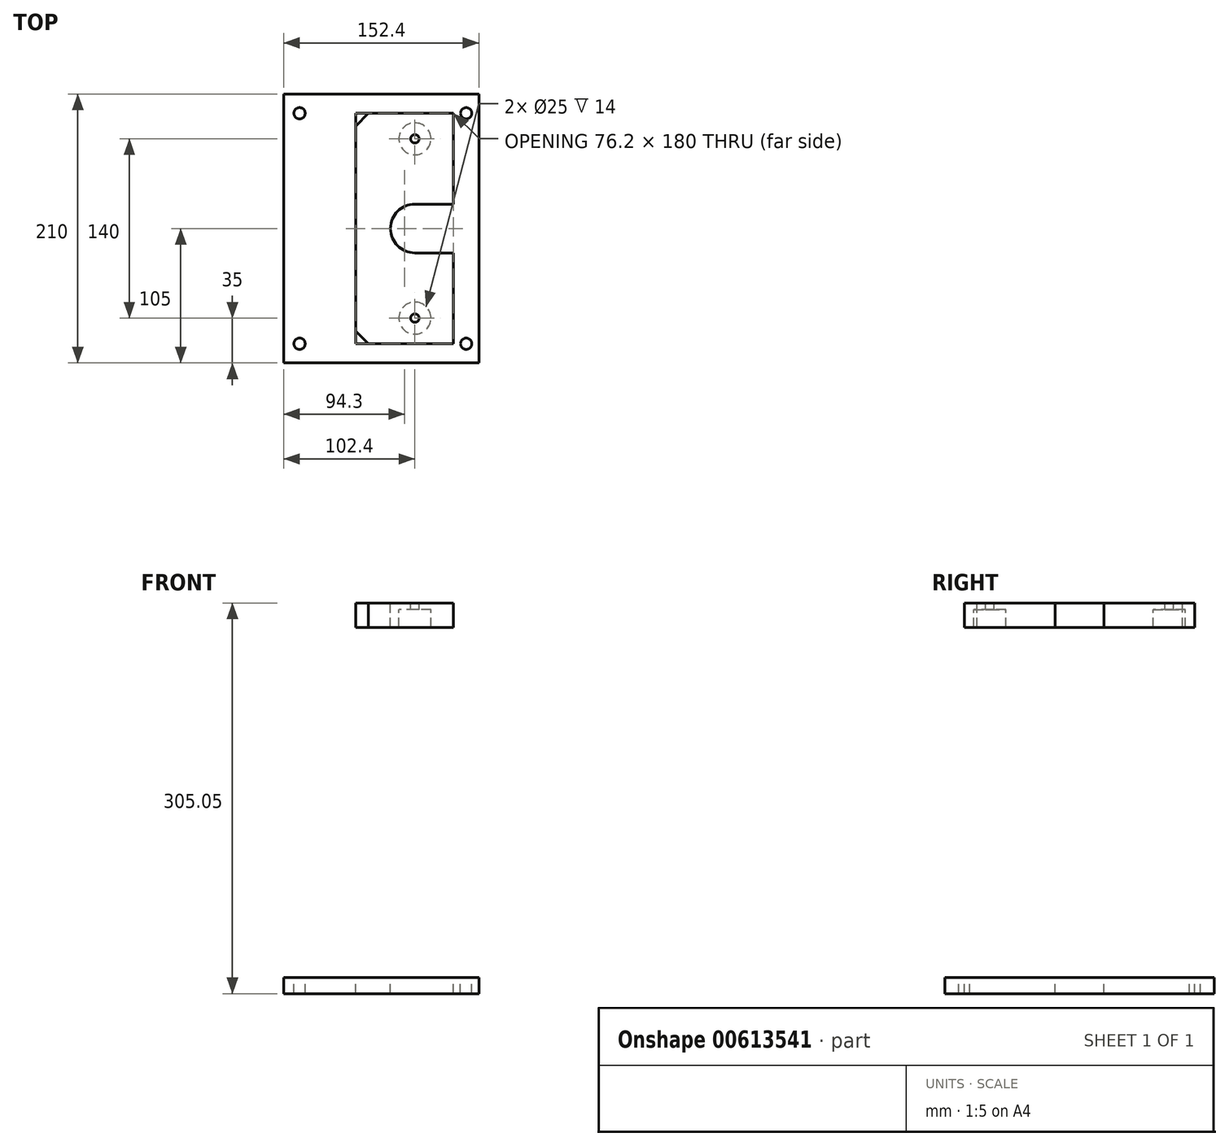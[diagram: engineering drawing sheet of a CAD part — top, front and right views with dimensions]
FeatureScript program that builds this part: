
annotation { "Feature Type Name" : "Feature", "Feature Type Description" : "" }
export const myFeature = defineFeature(function(context is Context, id is Id, definition is map)
    precondition{}
    {
        {
            var Q0;
            Q0=qCreatedBy(makeId("Top.planeOp"),FACE);
            cPlane(context, id + "F0", {"entities" : qUnion([Q0]), "cplaneType" : CPlaneType.OFFSET, "offset" : 12.7 * mm, "width" : 150 * mm, "height" : 150 * mm});
        }
        {
            var Q0;
            Q0=qCreatedBy(makeId("Top.planeOp"),FACE);
            cPlane(context, id + "F1", {"entities" : qUnion([Q0]), "cplaneType" : CPlaneType.OFFSET, "offset" : 300 * mm, "width" : 150 * mm, "height" : 150 * mm});
        }
        {
            var Q0;
            Q0=qCreatedBy(makeId("Top.planeOp"),FACE);
            var sketch = newSketch(context, id + "F2", { "sketchPlane" : qUnion([Q0])});
            skLineSegment(sketch, "E0.bottom", {"start": v(50, 105) * mm, "end": v(-102.4, 105) * mm});
            skLineSegment(sketch, "E0.top", {"start": v(50, -105) * mm, "end": v(-102.4, -105) * mm});
            skLineSegment(sketch, "E0.left", {"start": v(50, 105) * mm, "end": v(50, -105) * mm});
            skLineSegment(sketch, "E0.right", {"start": v(-102.4, 105) * mm, "end": v(-102.4, -105) * mm});
            skCircle(sketch, "E1", {"center": v(0, 70) * mm, "radius": 12.5 * mm, "construction": true});
            skCircle(sketch, "E2", {"center": v(0, -70) * mm, "radius": 12.5 * mm, "construction": true});
            skSolve(sketch);
        }
        {
            var Q0;
            Q0=qCreatedBy(id+"F1.planeOp",FACE);
            var sketch = newSketch(context, id + "F3", { "sketchPlane" : qUnion([Q0])});
            skLineSegment(sketch, "E3.bottom", {"start": v(30, 90) * mm, "end": v(-46.2, 90) * mm});
            skLineSegment(sketch, "E3.top", {"start": v(30, -90) * mm, "end": v(-46.2, -90) * mm});
            skLineSegment(sketch, "E3.left", {"start": v(30, 90) * mm, "end": v(30, 19.05) * mm});
            skLineSegment(sketch, "E3.right", {"start": v(-46.2, 90) * mm, "end": v(-46.2, -90) * mm});
            skArc(sketch, "E4", {"start": v(0, 19.05) * mm, "mid": v(-19.05, 0) * mm, "end": v(0, -19.05) * mm});
            skLineSegment(sketch, "E5", {"start": v(0, 19.05) * mm, "end": v(30, 19.05) * mm});
            skLineSegment(sketch, "E6", {"start": v(0, -19.05) * mm, "end": v(30, -19.05) * mm});
            skLineSegment(sketch, "E7.trimOffspring", {"start": v(30, -19.05) * mm, "end": v(30, -90) * mm});
            skSolve(sketch);
        }
        {
            var Q0;
            Q0 = qSketchRegion(id + "F2", true);
            var Q1;
            Q1=qCreatedBy(id+"F0.planeOp",FACE);
            extrude(context, id + "F4", {"entities" : qUnion([Q0]), "endBound" : BoundingType.UP_TO_SURFACE, "depth" : 12.7 * mm, "endBoundEntityFace" : qUnion([Q1]), "offsetDistance" : 25 * mm});
        }
        {
            var Q0;
            Q0=qCreatedBy(id+"F0.planeOp",FACE);
            var sketch = newSketch(context, id + "F5", { "sketchPlane" : qUnion([Q0])});
            skCircle(sketch, "E8", {"center": v(0, 70) * mm, "radius": 12.5 * mm});
            skCircle(sketch, "E9", {"center": v(0, -70) * mm, "radius": 12.5 * mm});
            skSolve(sketch);
        }
        {
            var Q0;
            Q0=makeQuery(id+"F5.imprint","IMPRINT",FACE,{"disambiguationData":[TD([[makeQuery(id+"F5.imprint","IMPRINT",EDGE,{"derivedFrom":sQuery(id+"F5.wireOp",EDGE,"E8")}),1.0]])]});
            var Q1;
            Q1=qCreatedBy(id+"F1.planeOp",FACE);
            extrude(context, id + "F6", {"entities" : qUnion([Q0]), "endBound" : BoundingType.UP_TO_SURFACE, "depth" : 25 * mm, "endBoundEntityFace" : qUnion([Q1]), "offsetDistance" : 25 * mm});
        }
        {
            var Q0;
            Q0=makeQuery(id+"F5.imprint","IMPRINT",FACE,{"disambiguationData":[TD([[makeQuery(id+"F5.imprint","IMPRINT",EDGE,{"derivedFrom":sQuery(id+"F5.wireOp",EDGE,"E9")}),1.0]])]});
            var Q1;
            Q1=qCreatedBy(id+"F1.planeOp",FACE);
            extrude(context, id + "F7", {"entities" : qUnion([Q0]), "endBound" : BoundingType.UP_TO_SURFACE, "depth" : 25 * mm, "endBoundEntityFace" : qUnion([Q1]), "offsetDistance" : 25 * mm});
        }
        {
            var Q0;
            Q0=makeQuery(id+"F6.opExtrude","CAP_EDGE",EDGE,{"disambiguationData":[OSD([sQuery(id+"F5.wireOp",EDGE,"E8")])],"isStart":true});
            var Q1;
            Q1=makeQuery(id+"F6.opExtrude","CAP_EDGE",EDGE,{"disambiguationData":[OSD([sQuery(id+"F5.wireOp",EDGE,"E8")])],"isStart":false});
            chamfer(context, id + "F8", {"entities" : qUnion([Q0, Q1]), "width" : 1 * mm, "tangentPropagation" : true});
        }
        {
            var Q0;
            Q0=makeQuery(id+"F7.opExtrude","CAP_EDGE",EDGE,{"disambiguationData":[OSD([sQuery(id+"F5.wireOp",EDGE,"E9")])],"isStart":true});
            var Q1;
            Q1=makeQuery(id+"F7.opExtrude","CAP_EDGE",EDGE,{"disambiguationData":[OSD([sQuery(id+"F5.wireOp",EDGE,"E9")])],"isStart":false});
            chamfer(context, id + "F9", {"entities" : qUnion([Q0, Q1]), "width" : 1 * mm, "tangentPropagation" : true});
        }
        {
            var Q0;
            Q0=sQuery(id+"F5.wireOp",VERTEX,"E8.center");
            var Q1;
            Q1=makeQuery(id+"F6.opExtrude","SWEPT_BODY",BODY,{"disambiguationData":[OSD([sQuery(id+"F5.wireOp",EDGE,"E8")])]});
            hole(context, id + "F10", {"style" : HoleStyle.SIMPLE, "endStyle" : HoleEndStyle.BLIND, "oppositeDirection" : true, "standardTappedOrClearance" : lookupTablePath({ "standard" : "ISO", "engagement" : "75%", "pitch" : "1 mm", "size" : "M6", "type" : "Tapped" }), "standardBlindInLast" : lookupTablePath({ "standard" : "ISO", "engagement" : "75%", "pitch" : "1 mm", "size" : "M6", "type" : "Tapped" }), "holeDiameter" : 5 * mm, "majorDiameter" : 6 * mm, "showTappedDepth" : true, "holeDepth" : 15 * mm, "isTappedThrough" : true, "tappedDepth" : 12 * mm, "tapClearance" : 3, "locations" : qUnion([Q0]), "scope" : qUnion([Q1])});
        }
        {
            var Q0;
            Q0=sQuery(id+"F5.wireOp",VERTEX,"E9.center");
            var Q1;
            Q1=makeQuery(id+"F7.opExtrude","SWEPT_BODY",BODY,{"disambiguationData":[OSD([sQuery(id+"F5.wireOp",EDGE,"E9")])]});
            hole(context, id + "F11", {"style" : HoleStyle.SIMPLE, "endStyle" : HoleEndStyle.BLIND, "oppositeDirection" : true, "standardTappedOrClearance" : lookupTablePath({ "standard" : "ISO", "engagement" : "75%", "pitch" : "1 mm", "size" : "M6", "type" : "Tapped" }), "standardBlindInLast" : lookupTablePath({ "standard" : "ISO", "engagement" : "75%", "pitch" : "1 mm", "size" : "M6", "type" : "Tapped" }), "holeDiameter" : 5 * mm, "majorDiameter" : 6 * mm, "showTappedDepth" : true, "holeDepth" : 15 * mm, "isTappedThrough" : true, "tappedDepth" : 12 * mm, "tapClearance" : 3, "locations" : qUnion([Q0]), "scope" : qUnion([Q1])});
        }
        {
            var Q0;
            Q0=sQuery(id+"F2.wireOp",VERTEX,"E2.center");
            var Q1;
            Q1=sQuery(id+"F2.wireOp",VERTEX,"E1.center");
            var Q2;
            Q2=makeQuery(id+"F4.opExtrude","SWEPT_BODY",BODY,{"disambiguationData":[OSD([sQuery(id+"F2.wireOp",EDGE,"E0.bottom"),sQuery(id+"F2.wireOp",EDGE,"E0.top"),sQuery(id+"F2.wireOp",EDGE,"E0.left"),sQuery(id+"F2.wireOp",EDGE,"E0.right")])]});
            hole(context, id + "F12", {"style" : HoleStyle.C_BORE, "endStyle" : HoleEndStyle.BLIND, "oppositeDirection" : true, "standardTappedOrClearance" : lookupTablePath({ "standard" : "ISO", "fit" : "Normal", "size" : "M6", "type" : "Clearance" }), "standardBlindInLast" : lookupTablePath({ "fit" : "Standard", "standard" : "ISO", "size" : "M6", "type" : "Clearance" }), "holeDiameter" : 6.6 * mm, "cBoreDiameter" : 11.25 * mm, "cBoreDepth" : 6 * mm, "majorDiameter" : 5 * mm, "holeDepth" : 15 * mm, "isTappedThrough" : true, "tappedDepth" : 12 * mm, "tapClearance" : 3, "startFromSketch" : true, "locations" : qUnion([Q0, Q1]), "scope" : qUnion([Q2])});
        }
        {
            var Q0;
            Q0=makeQuery(id+"F6.opExtrude","CAP_FACE",FACE,{"disambiguationData":[OSD([sQuery(id+"F5.wireOp",EDGE,"E8")])],"isStart":false});
            var sketch = newSketch(context, id + "F13", { "sketchPlane" : qUnion([Q0])});
            skPoint(sketch, "E10", {"position": v(0, -70.15) * mm});
            skPoint(sketch, "E11", {"position": v(0, 70) * mm});
            skSolve(sketch);
        }
        {
            var Q0;
            Q0=sQuery(id+"F13.wireOp",VERTEX,"E10");
            var Q1;
            Q1=sQuery(id+"F13.wireOp",VERTEX,"E11");
            var Q2;
            Q2=makeQuery(id+"F6.opExtrude","SWEPT_BODY",BODY,{"disambiguationData":[OSD([sQuery(id+"F5.wireOp",EDGE,"E8")])]});
            var Q3;
            Q3=makeQuery(id+"F7.opExtrude","SWEPT_BODY",BODY,{"disambiguationData":[OSD([sQuery(id+"F5.wireOp",EDGE,"E9")])]});
            hole(context, id + "F14", {"style" : HoleStyle.SIMPLE, "endStyle" : HoleEndStyle.BLIND, "standardTappedOrClearance" : lookupTablePath({ "standard" : "ISO", "engagement" : "75%", "pitch" : "1 mm", "size" : "M6", "type" : "Tapped" }), "standardBlindInLast" : lookupTablePath({ "standard" : "ISO", "engagement" : "75%", "pitch" : "1 mm", "size" : "M6", "type" : "Tapped" }), "holeDiameter" : 5 * mm, "majorDiameter" : 6 * mm, "showTappedDepth" : true, "holeDepth" : 15 * mm, "isTappedThrough" : true, "tappedDepth" : 12 * mm, "tapClearance" : 3, "startFromSketch" : true, "locations" : qUnion([Q0, Q1]), "scope" : qUnion([Q2, Q3])});
        }
        {
            var Q0;
            Q0 = qSketchRegion(id + "F3", true);
            extrude(context, id + "F15", {"entities" : qUnion([Q0]), "oppositeDirection" : true, "depth" : 14 * mm, "offsetDistance" : 25 * mm, "hasSecondDirection" : true, "secondDirectionOppositeDirection" : false, "secondDirectionDepth" : 5.05 * mm});
        }
        {
            var Q0;
            Q0=qCreatedBy(id+"F1.planeOp",FACE);
            var sketch = newSketch(context, id + "F16", { "sketchPlane" : qUnion([Q0])});
            skCircle(sketch, "E12", {"center": v(0, -70) * mm, "radius": 12.5 * mm});
            skCircle(sketch, "E13", {"center": v(0, 70) * mm, "radius": 12.5 * mm});
            skSolve(sketch);
        }
        {
            var Q0;
            Q0 = qSketchRegion(id + "F16", true);
            var Q1;
            Q1=makeQuery(id+"F15.opExtrude","CAP_FACE",FACE,{"disambiguationData":[OSD([sQuery(id+"F3.wireOp",EDGE,"E3.bottom"),sQuery(id+"F3.wireOp",EDGE,"E3.top"),sQuery(id+"F3.wireOp",EDGE,"E3.left"),sQuery(id+"F3.wireOp",EDGE,"E3.right"),sQuery(id+"F3.wireOp",EDGE,"E4"),sQuery(id+"F3.wireOp",EDGE,"E5"),sQuery(id+"F3.wireOp",EDGE,"E6"),sQuery(id+"F3.wireOp",EDGE,"E7.trimOffspring")])],"isStart":false});
            extrude(context, id + "F17", {"entities" : qUnion([Q0, Q1]), "operationType" : NewBodyOperationType.REMOVE, "endBound" : BoundingType.THROUGH_ALL, "oppositeDirection" : true, "depth" : 25 * mm, "offsetDistance" : 25 * mm});
        }
        {
            var Q0;
            Q0=makeQuery(id+"F15.opExtrude","CAP_FACE",FACE,{"disambiguationData":[OSD([sQuery(id+"F3.wireOp",EDGE,"E3.bottom"),sQuery(id+"F3.wireOp",EDGE,"E3.top"),sQuery(id+"F3.wireOp",EDGE,"E3.left"),sQuery(id+"F3.wireOp",EDGE,"E3.right"),sQuery(id+"F3.wireOp",EDGE,"E4"),sQuery(id+"F3.wireOp",EDGE,"E5"),sQuery(id+"F3.wireOp",EDGE,"E6"),sQuery(id+"F3.wireOp",EDGE,"E7.trimOffspring")])],"isStart":true});
            var sketch = newSketch(context, id + "F18", { "sketchPlane" : qUnion([Q0])});
            skPoint(sketch, "E14", {"position": v(0, 70) * mm});
            skPoint(sketch, "E15", {"position": v(0, -70) * mm});
            skSolve(sketch);
        }
        {
            var Q0;
            Q0=sQuery(id+"F18.wireOp",VERTEX,"E14");
            var Q1;
            Q1=sQuery(id+"F18.wireOp",VERTEX,"E15");
            var Q2;
            Q2=makeQuery(id+"F15.opExtrude","SWEPT_BODY",BODY,{"disambiguationData":[OSD([sQuery(id+"F3.wireOp",EDGE,"E3.bottom"),sQuery(id+"F3.wireOp",EDGE,"E3.top"),sQuery(id+"F3.wireOp",EDGE,"E3.left"),sQuery(id+"F3.wireOp",EDGE,"E3.right"),sQuery(id+"F3.wireOp",EDGE,"E4"),sQuery(id+"F3.wireOp",EDGE,"E5"),sQuery(id+"F3.wireOp",EDGE,"E6"),sQuery(id+"F3.wireOp",EDGE,"E7.trimOffspring")])]});
            hole(context, id + "F19", {"style" : HoleStyle.SIMPLE, "endStyle" : HoleEndStyle.THROUGH, "standardTappedOrClearance" : lookupTablePath({ "standard" : "ISO", "fit" : "Normal", "size" : "M6", "type" : "Clearance" }), "standardBlindInLast" : lookupTablePath({ "fit" : "Standard", "standard" : "ISO", "size" : "M6", "type" : "Clearance" }), "holeDiameter" : 6.6 * mm, "majorDiameter" : 6 * mm, "isTappedThrough" : true, "tappedDepth" : 12 * mm, "tapClearance" : 3, "startFromSketch" : true, "locations" : qUnion([Q0, Q1]), "scope" : qUnion([Q2])});
        }
        {
            var Q0;
            Q0=makeQuery(id+"F15.opExtrude","SWEPT_EDGE",EDGE,{"disambiguationData":[OSD([sQuery(id+"F3.wireOp",EDGE,"E3.bottom"),sQuery(id+"F3.wireOp",EDGE,"E3.right")])]});
            var Q1;
            Q1=makeQuery(id+"F15.opExtrude","SWEPT_EDGE",EDGE,{"disambiguationData":[OSD([sQuery(id+"F3.wireOp",EDGE,"E3.top"),sQuery(id+"F3.wireOp",EDGE,"E3.right")])]});
            chamfer(context, id + "F20", {"entities" : qUnion([Q0, Q1]), "width" : 10 * mm, "tangentPropagation" : true});
        }
        {
            var Q0;
            Q0=makeQuery(id+"F4.opExtrude","CAP_FACE",FACE,{"disambiguationData":[OSD([sQuery(id+"F2.wireOp",EDGE,"E0.bottom"),sQuery(id+"F2.wireOp",EDGE,"E0.top"),sQuery(id+"F2.wireOp",EDGE,"E0.left"),sQuery(id+"F2.wireOp",EDGE,"E0.right")])],"isStart":false});
            var sketch = newSketch(context, id + "F21", { "sketchPlane" : qUnion([Q0])});
            skPoint(sketch, "E16", {"position": v(-90, 90) * mm});
            skPoint(sketch, "E17", {"position": v(40, 90) * mm});
            skPoint(sketch, "E18", {"position": v(-90, -90) * mm});
            skPoint(sketch, "E19", {"position": v(40, -90) * mm});
            skLineSegment(sketch, "E20", {"start": v(0, 0) * mm, "end": v(-102.4, 0) * mm, "construction": true});
            skLineSegment(sketch, "E21", {"start": v(0, 0) * mm, "end": v(0, 105) * mm, "construction": true});
            skSolve(sketch);
        }
        {
            var Q0;
            Q0=sQuery(id+"F21.wireOp",VERTEX,"E16");
            var Q1;
            Q1=sQuery(id+"F21.wireOp",VERTEX,"E18");
            var Q2;
            Q2=sQuery(id+"F21.wireOp",VERTEX,"E19");
            var Q3;
            Q3=sQuery(id+"F21.wireOp",VERTEX,"E17");
            var Q4;
            Q4=makeQuery(id+"F4.opExtrude","SWEPT_BODY",BODY,{"disambiguationData":[OSD([sQuery(id+"F2.wireOp",EDGE,"E0.bottom"),sQuery(id+"F2.wireOp",EDGE,"E0.top"),sQuery(id+"F2.wireOp",EDGE,"E0.left"),sQuery(id+"F2.wireOp",EDGE,"E0.right")])]});
            hole(context, id + "F22", {"style" : HoleStyle.SIMPLE, "endStyle" : HoleEndStyle.THROUGH, "standardTappedOrClearance" : lookupTablePath({ "standard" : "ISO", "fit" : "Normal", "size" : "M8", "type" : "Clearance" }), "standardBlindInLast" : lookupTablePath({ "fit" : "Standard", "standard" : "ISO", "size" : "M8", "type" : "Clearance" }), "holeDiameter" : 8.8 * mm, "majorDiameter" : 5 * mm, "isTappedThrough" : true, "tappedDepth" : 12 * mm, "tapClearance" : 3, "startFromSketch" : true, "locations" : qUnion([Q0, Q1, Q2, Q3]), "scope" : qUnion([Q4])});
        }
    });
